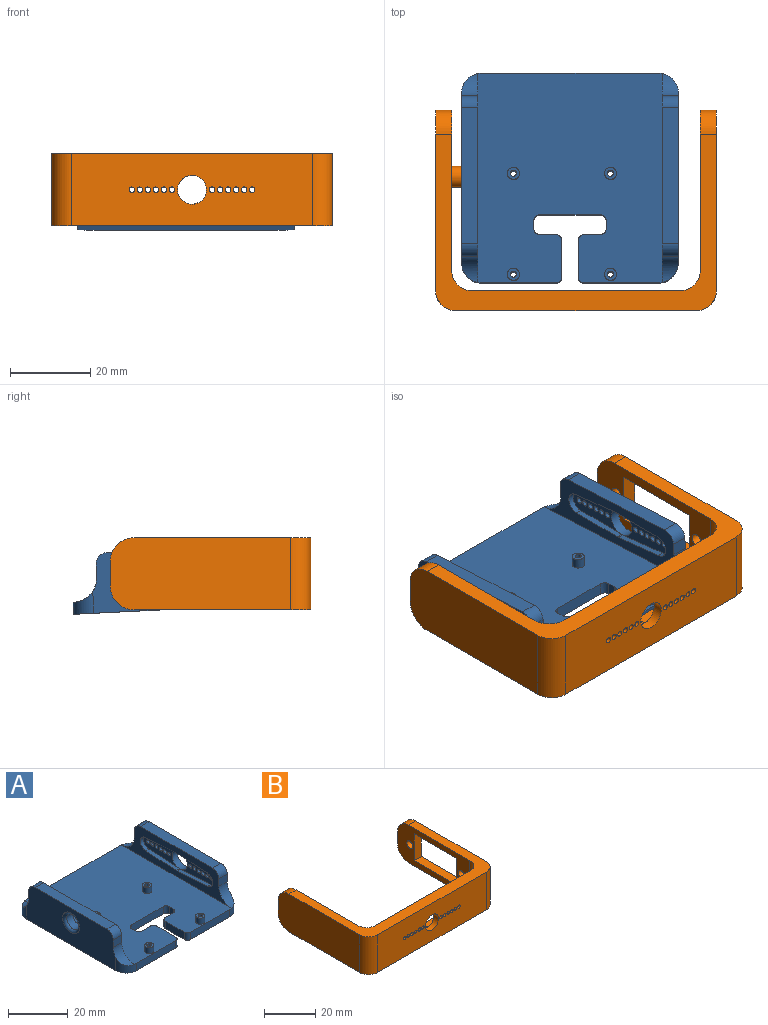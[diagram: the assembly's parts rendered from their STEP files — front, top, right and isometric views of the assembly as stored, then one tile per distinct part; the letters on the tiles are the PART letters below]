
ASSEMBLY  parts=2 mates=1
PART A: 77 faces, bbox 54x52.3x15 mm
  f0: plane 52.3x46.43mm, normal (0,0,1), area 2239.4mm2, adj f1,f3,f8,f11,f13,f15,f17,f19
  f1: plane 18.5x3mm, normal (0,-1,0), area 55.5mm2, adj f0,f10,f32,f74
  f2: plane 42.3x15mm, normal (-1,0,0), area 561mm2, adj f10,f39,f40,f41,f65,f66,f69,f70
  f3: plane 18.5x3mm, normal (0,-1,0), area 55.5mm2, adj f0,f10,f33,f73
  f4: plane 42.3x15mm, normal (1,0,0), area 552.1mm2, adj f10,f35,f36,f37,f42,f43,f44,f45
  f5: cylinder r=0.75mm len=5.5mm, axis (0,0,1), area 25.9mm2, adj f10,f14
  f6: cylinder r=0.75mm len=5.5mm, axis (0,0,1), area 25.9mm2, adj f10,f16
  f7: cylinder r=0.75mm len=5.5mm, axis (0,0,1), area 25.9mm2, adj f10,f18
  f8: plane 44x3mm, normal (0,1,0), area 132mm2, adj f0,f10,f71,f72
  f9: cylinder r=0.75mm len=5.5mm, axis (0,0,1), area 25.9mm2, adj f10,f12
  f10: plane 54x52.3mm, normal (0,0,-1), area 2657.7mm2, adj f1,f2,f3,f4,f5,f6,f7,f8
  f11: cylinder r=1.5mm len=3mm, axis (0,0,-1), area 23.6mm2, adj f0,f12
  f12: plane 3x3mm, normal (0,0,1), area 5.3mm2, adj f9,f11
  f13: cylinder r=1.5mm len=3mm, axis (0,0,-1), area 23.6mm2, adj f0,f14
  f14: plane 3x3mm, normal (0,0,1), area 5.3mm2, adj f5,f13
  f15: cylinder r=1.5mm len=3mm, axis (0,0,-1), area 23.6mm2, adj f0,f16
  f16: plane 3x3mm, normal (0,0,1), area 5.3mm2, adj f6,f15
  f17: cylinder r=1.5mm len=3mm, axis (0,0,-1), area 23.6mm2, adj f0,f18
  f18: plane 3x3mm, normal (0,0,1), area 5.3mm2, adj f7,f17
  f19: plane 9x3mm, normal (-1,0,0), area 27mm2, adj f0,f10,f26,f32
  f20: plane 4x3mm, normal (0,1,0), area 12mm2, adj f0,f10,f26,f27
  f21: plane 3x2mm, normal (-1,0,0), area 6mm2, adj f0,f10,f27,f28
  f22: plane 15x3mm, normal (0,-1,0), area 45mm2, adj f0,f10,f28,f29
  f23: plane 3x2mm, normal (1,0,0), area 6mm2, adj f0,f10,f29,f30
  f24: plane 4x3mm, normal (0,1,0), area 12mm2, adj f0,f10,f30,f31
  f25: plane 9x3mm, normal (1,0,0), area 27mm2, adj f0,f10,f31,f33
  f26: cylinder r=1.5mm len=3mm, axis (0,0,-1), area 7.1mm2, adj f0,f10,f19,f20
  f27: cylinder r=1.5mm len=3mm, axis (0,0,1), area 7.1mm2, adj f0,f10,f20,f21
  f28: cylinder r=1.5mm len=3mm, axis (0,0,-1), area 7.1mm2, adj f0,f10,f21,f22
  f29: cylinder r=1.5mm len=3mm, axis (0,0,1), area 7.1mm2, adj f0,f10,f22,f23
  f30: cylinder r=1.5mm len=3mm, axis (0,0,-1), area 7.1mm2, adj f0,f10,f23,f24
  f31: cylinder r=1.5mm len=3mm, axis (0,0,1), area 7.1mm2, adj f0,f10,f24,f25
  f32: cylinder r=1.5mm len=3mm, axis (0,0,-1), area 7.1mm2, adj f0,f1,f10,f19
  f33: cylinder r=1.5mm len=3mm, axis (0,0,1), area 7.1mm2, adj f0,f3,f10,f25
  f34: plane 52x12mm, normal (-1,0,0), area 285.3mm2, adj f0,f35,f36,f37,f48,f55,f56,f57
  f35: plane 4x3mm, normal (0,-1,0), area 12mm2, adj f4,f34,f63,f67
  f36: plane 4x3mm, normal (0,1,0), area 12mm2, adj f4,f34,f64,f68
  f37: plane 34x4mm, normal (0,0,1), area 136mm2, adj f4,f34,f67,f68
  f38: plane 52x12mm, normal (1,0,0), area 463.3mm2, adj f0,f39,f40,f41,f65,f66,f69,f70
  f39: plane 4x3mm, normal (0,1,0), area 12mm2, adj f2,f38,f65,f69
  f40: plane 4x3mm, normal (0,-1,0), area 12mm2, adj f2,f38,f66,f70
  f41: plane 34x4mm, normal (0,0,1), area 136mm2, adj f2,f38,f69,f70
  f42: cylinder r=0.7mm len=2.5mm, axis (-1,0,0), area 11mm2, adj f4,f58
  f43: cylinder r=0.7mm len=2.5mm, axis (-1,0,0), area 11mm2, adj f4,f58
  f44: cylinder r=0.7mm len=2.5mm, axis (-1,0,0), area 11mm2, adj f4,f58
  f45: cylinder r=0.7mm len=2.5mm, axis (-1,0,0), area 11mm2, adj f4,f58
  f46: cylinder r=0.7mm len=2.5mm, axis (-1,0,0), area 11mm2, adj f4,f58
  f47: cylinder r=0.7mm len=2.5mm, axis (-1,0,0), area 11mm2, adj f4,f58
  f48: cylinder r=3.6mm len=7.2mm, axis (-1,0,0), area 57.8mm2, adj f4,f34,f56,f57,f58,f59,f61,f62
  f49: cylinder r=0.7mm len=2.5mm, axis (-1,0,0), area 11mm2, adj f4,f62
  f50: cylinder r=0.7mm len=2.5mm, axis (-1,0,0), area 11mm2, adj f4,f62
  f51: cylinder r=0.7mm len=2.5mm, axis (-1,0,0), area 11mm2, adj f4,f62
  f52: cylinder r=0.7mm len=2.5mm, axis (-1,0,0), area 11mm2, adj f4,f62
  f53: cylinder r=0.7mm len=2.5mm, axis (-1,0,0), area 11mm2, adj f4,f62
  f54: cylinder r=0.7mm len=2.5mm, axis (-1,0,0), area 11mm2, adj f4,f62
  f55: cylinder r=2.75mm len=5.49mm, axis (-1,0,0), area 12.5mm2, adj f34,f56,f57,f58
  f56: plane 14.3x1.5mm, normal (0,0.06,-1), area 21.5mm2, adj f34,f48,f55,f58
  f57: plane 14.3x1.5mm, normal (0,0.06,1), area 21.5mm2, adj f34,f48,f55,f58
  f58: plane 16.89x7.19mm, normal (-1,0,0), area 73.6mm2, adj f42,f43,f44,f45,f46,f47,f48,f55
  f59: plane 14.3x1.5mm, normal (0,-0.06,-1), area 21.5mm2, adj f34,f48,f60,f62
  f60: cylinder r=2.75mm len=5.49mm, axis (-1,0,0), area 12.5mm2, adj f34,f59,f61,f62
  f61: plane 14.3x1.5mm, normal (0,-0.06,1), area 21.5mm2, adj f34,f48,f60,f62
  f62: plane 16.89x7.19mm, normal (-1,0,0), area 73.6mm2, adj f48,f49,f50,f51,f52,f53,f54,f59
  f63: cylinder r=6mm len=6mm, axis (1,0,0), area 32.8mm2, adj f0,f4,f34,f35,f74
  f64: cylinder r=6mm len=6mm, axis (-1,0,0), area 32.8mm2, adj f0,f4,f34,f36,f71
  f65: cylinder r=6mm len=6mm, axis (-1,0,0), area 32.8mm2, adj f0,f2,f38,f39,f72
  f66: cylinder r=6mm len=6mm, axis (1,0,0), area 32.8mm2, adj f0,f2,f38,f40,f73
  f67: cylinder r=3mm len=4mm, axis (-1,0,0), area 18.8mm2, adj f4,f34,f35,f37
  f68: cylinder r=3mm len=4mm, axis (1,0,0), area 18.8mm2, adj f4,f34,f36,f37
  f69: cylinder r=3mm len=4mm, axis (1,0,0), area 18.8mm2, adj f2,f38,f39,f41
  f70: cylinder r=3mm len=4mm, axis (-1,0,0), area 18.8mm2, adj f2,f38,f40,f41
  f71: cylinder r=5mm len=5.47mm, axis (0,0,-1), area 27.4mm2, adj f0,f4,f8,f10,f64
  f72: cylinder r=5mm len=5.47mm, axis (0,0,1), area 27.4mm2, adj f0,f2,f8,f10,f65
  f73: cylinder r=5mm len=5.47mm, axis (0,0,1), area 27.4mm2, adj f0,f2,f3,f10,f66
  f74: cylinder r=5mm len=5.47mm, axis (0,0,-1), area 27.4mm2, adj f0,f1,f4,f10,f63
  f75: cylinder r=3mm len=6mm, axis (-1,0,0), area 56.5mm2, adj f38,f76
  f76: torus R=4mm, axis (1,0,0), area 33.2mm2, adj f2,f75
PART B: 48 faces, bbox 70x50x18 mm
  f0: plane 52x18mm, normal (0,1,0), area 729.7mm2, adj f8,f9,f25,f38,f39,f40,f42,f43
  f1: plane 45x18mm, normal (1,0,0), area 476.6mm2, adj f5,f8,f9,f13,f14,f15,f16,f17
  f2: plane 40x18mm, normal (-1,0,0), area 386.6mm2, adj f5,f8,f9,f13,f14,f15,f16,f17
  f3: plane 45x18mm, normal (-1,0,0), area 794.5mm2, adj f7,f8,f9,f19,f21,f23
  f4: plane 60x18mm, normal (0,-1,0), area 1020.8mm2, adj f8,f9,f23,f24,f25,f26,f27,f28
  f5: plane 6x4mm, normal (0,1,0), area 24mm2, adj f1,f2,f20,f22
  f6: plane 40x18mm, normal (1,0,0), area 683.3mm2, adj f7,f8,f9,f10,f19,f21,f46
  f7: plane 6x4mm, normal (0,1,0), area 24mm2, adj f3,f6,f19,f21
  f8: plane 70x44mm, normal (0,0,1), area 662mm2, adj f0,f1,f2,f3,f4,f6,f21,f22
  f9: plane 70x44mm, normal (0,0,-1), area 662mm2, adj f0,f1,f2,f3,f4,f6,f19,f20
  f10: cylinder r=2.6mm len=5.5mm, axis (-1,0,0), area 89.8mm2, adj f6,f12
  f11: plane 3.2x3.2mm, normal (1,0,0), area 8mm2, adj f12
  f12: torus R=1.6mm, axis (1,0,0), area 22.1mm2, adj f10,f11
  f13: plane 12.8x4mm, normal (0,-1,0), area 51.2mm2, adj f1,f2,f14,f15
  f14: plane 23.5x4mm, normal (0,0,1), area 94mm2, adj f1,f2,f13,f16
  f15: plane 23.5x4mm, normal (0,0,-1), area 94mm2, adj f1,f2,f13,f16
  f16: plane 12.8x4mm, normal (0,1,0), area 51.2mm2, adj f1,f2,f14,f15
  f17: cylinder r=1.65mm len=4mm, axis (1,0,0), area 41.5mm2, adj f1,f2
  f18: cylinder r=1.65mm len=4mm, axis (1,0,0), area 41.5mm2, adj f1,f2
  f19: cylinder r=6mm len=6mm, axis (-1,0,0), area 37.7mm2, adj f3,f6,f7,f9
  f20: cylinder r=6mm len=6mm, axis (-1,0,0), area 37.7mm2, adj f1,f2,f5,f9
  f21: cylinder r=6mm len=6mm, axis (1,0,0), area 37.7mm2, adj f3,f6,f7,f8
  f22: cylinder r=6mm len=6mm, axis (1,0,0), area 37.7mm2, adj f1,f2,f5,f8
  f23: cylinder r=5mm len=18mm, axis (0,0,1), area 141.4mm2, adj f3,f4,f8,f9
  f24: cylinder r=5mm len=18mm, axis (0,0,1), area 141.4mm2, adj f1,f4,f8,f9
  f25: cylinder r=3.6mm len=7.2mm, axis (0,1,0), area 58.7mm2, adj f0,f4,f38,f40,f41,f42,f44,f45
  f26: cylinder r=0.7mm len=2.5mm, axis (0,1,0), area 11mm2, adj f4,f45
  f27: cylinder r=0.7mm len=2.5mm, axis (0,1,0), area 11mm2, adj f4,f45
  f28: cylinder r=0.7mm len=2.5mm, axis (0,1,0), area 11mm2, adj f4,f45
  f29: cylinder r=0.7mm len=2.5mm, axis (0,1,0), area 11mm2, adj f4,f45
  f30: cylinder r=0.7mm len=2.5mm, axis (0,1,0), area 11mm2, adj f4,f45
  f31: cylinder r=0.7mm len=2.5mm, axis (0,1,0), area 11mm2, adj f4,f45
  f32: cylinder r=0.7mm len=2.5mm, axis (0,1,0), area 11mm2, adj f4,f41
  f33: cylinder r=0.7mm len=2.5mm, axis (0,1,0), area 11mm2, adj f4,f41
  f34: cylinder r=0.7mm len=2.5mm, axis (0,1,0), area 11mm2, adj f4,f41
  f35: cylinder r=0.7mm len=2.5mm, axis (0,1,0), area 11mm2, adj f4,f41
  f36: cylinder r=0.7mm len=2.5mm, axis (0,1,0), area 11mm2, adj f4,f41
  f37: cylinder r=0.7mm len=2.5mm, axis (0,1,0), area 11mm2, adj f4,f41
  f38: plane 14.3x2.5mm, normal (0.06,0,1), area 35.8mm2, adj f0,f25,f39,f41
  f39: cylinder r=2.75mm len=5.49mm, axis (0,1,0), area 20.8mm2, adj f0,f38,f40,f41
  f40: plane 14.3x2.5mm, normal (0.06,0,-1), area 35.8mm2, adj f0,f25,f39,f41
  f41: plane 16.89x7.19mm, normal (0,1,0), area 73.6mm2, adj f25,f32,f33,f34,f35,f36,f37,f38
  f42: plane 14.3x2.5mm, normal (-0.06,0,-1), area 35.8mm2, adj f0,f25,f43,f45
  f43: cylinder r=2.75mm len=5.49mm, axis (0,1,0), area 20.8mm2, adj f0,f42,f44,f45
  f44: plane 14.3x2.5mm, normal (-0.06,0,1), area 35.8mm2, adj f0,f25,f43,f45
  f45: plane 16.89x7.19mm, normal (0,1,0), area 73.6mm2, adj f25,f26,f27,f28,f29,f30,f31,f42
  f46: cylinder r=5mm len=18mm, axis (0,0,-1), area 141.4mm2, adj f0,f6,f8,f9
  f47: cylinder r=5mm len=18mm, axis (0,0,1), area 141.4mm2, adj f0,f2,f8,f9
PLACE A rot(axis=(-1,0,0),2.9deg) t=(-16.42,23.92,-20.59)mm
PLACE B t=(-14.92,4.94,-24.39)mm
MATE revolute B.f12 <-> A.f38  axis (1,0,0) through (-39.42,35.84,-15.39)mm
